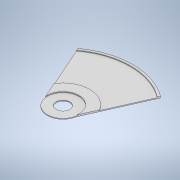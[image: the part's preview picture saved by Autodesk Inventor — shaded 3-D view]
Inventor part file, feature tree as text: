
AUTODESK INVENTOR PART (.ipt)
format: ipt  version: 2021 (Build 250183000, 183)  size: 133,632 bytes
history: native  units: mm
features: extrude x3, sketch x3
ambient origin geometry x8: Origin, YZ Plane, XZ Plane, XY Plane, X Axis, Y Axis, Z Axis, Center Point
bodies: Solid1 (feature_tree)
feature tree (6):
  extrude  "Extrusion1"  Depth=30.0mm
  extrude  "Extrusion2"  Depth=20.0mm
  extrude  "Extrusion3"  Depth=0.4mm
  sketch  "Sketch1"  dims[d0=149.0mm d3=30.0mm]
  sketch  "Sketch2"  dims[d4=8.6mm d5=20.0mm]
  sketch  "Sketch3"  dims[d6=1.0mm d7=0.0mm d8=20.4mm d9=0.5mm d10=0.0mm d12=43.0mm d13=17.0mm d14=0.4mm d15=0.0mm]
